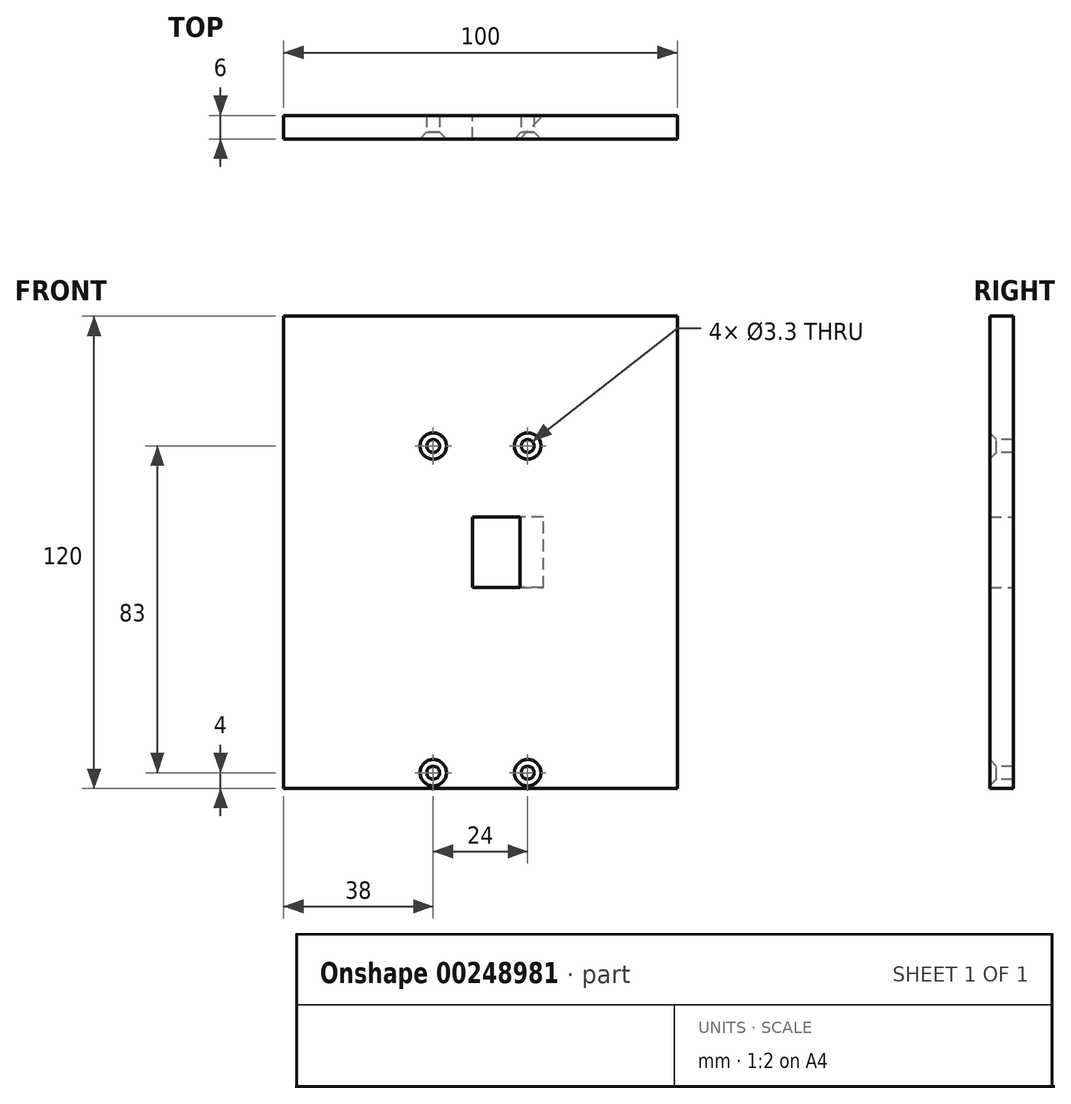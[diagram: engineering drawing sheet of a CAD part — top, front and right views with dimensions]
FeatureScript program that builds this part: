
annotation { "Feature Type Name" : "Feature", "Feature Type Description" : "" }
export const myFeature = defineFeature(function(context is Context, id is Id, definition is map)
    precondition{}
    {
        {
            var Q0;
            Q0=qCreatedBy(makeId("Front.planeOp"),FACE);
            var sketch = newSketch(context, id + "F0", { "sketchPlane" : qUnion([Q0])});
            skLineSegment(sketch, "E0.bottom", {"start": v(50, 60) * mm, "end": v(-50, 60) * mm});
            skLineSegment(sketch, "E0.top", {"start": v(50, -60) * mm, "end": v(-50, -60) * mm});
            skLineSegment(sketch, "E0.left", {"start": v(50, 60) * mm, "end": v(50, -60) * mm});
            skLineSegment(sketch, "E0.right", {"start": v(-50, 60) * mm, "end": v(-50, -60) * mm});
            skPoint(sketch, "E0.middle", {"position": v(0, 0) * mm});
            skLineSegment(sketch, "E1.bottom", {"start": v(10, -9) * mm, "end": v(-2, -9) * mm});
            skLineSegment(sketch, "E1.top", {"start": v(10, 9) * mm, "end": v(-2, 9) * mm});
            skLineSegment(sketch, "E1.left", {"start": v(10, -9) * mm, "end": v(10, 9) * mm});
            skLineSegment(sketch, "E1.right", {"start": v(-2, -9) * mm, "end": v(-2, 9) * mm});
            skPoint(sketch, "E1.middle", {"position": v(4, 0) * mm});
            skSolve(sketch);
        }
        {
            var Q0;
            Q0=makeQuery(id+"F0.imprint","IMPRINT",FACE,{"disambiguationData":[TD([[makeQuery(id+"F0.imprint","IMPRINT",EDGE,{"derivedFrom":sQuery(id+"F0.wireOp",EDGE,"E0.bottom")}),1.0]])]});
            extrude(context, id + "F1", {"entities" : qUnion([Q0]), "endBound" : BoundingType.SYMMETRIC, "depth" : 6 * mm});
        }
        {
            var Q0;
            Q0=makeQuery(id+"F1.opExtrude","CAP_EDGE",EDGE,{"disambiguationData":[OSD([sQuery(id+"F0.wireOp",EDGE,"E1.left")])],"isStart":true});
            chamfer(context, id + "F2", {"entities" : qUnion([Q0]), "width" : 6 * mm, "tangentPropagation" : true});
        }
        {
            var Q0;
            Q0=makeQuery(id+"F1.opExtrude","CAP_FACE",FACE,{"disambiguationData":[OSD([sQuery(id+"F0.wireOp",EDGE,"E0.bottom"),sQuery(id+"F0.wireOp",EDGE,"E0.top"),sQuery(id+"F0.wireOp",EDGE,"E0.left"),sQuery(id+"F0.wireOp",EDGE,"E0.right"),sQuery(id+"F0.wireOp",EDGE,"E1.bottom"),sQuery(id+"F0.wireOp",EDGE,"E1.top"),sQuery(id+"F0.wireOp",EDGE,"E1.left"),sQuery(id+"F0.wireOp",EDGE,"E1.right")])],"isStart":false});
            var sketch = newSketch(context, id + "F3", { "sketchPlane" : qUnion([Q0])});
            skPoint(sketch, "E2", {"position": v(-12, -56) * mm});
            skPoint(sketch, "E3", {"position": v(12, -56) * mm});
            skPoint(sketch, "E4", {"position": v(-12, 27) * mm});
            skPoint(sketch, "E5", {"position": v(12, 27) * mm});
            skSolve(sketch);
        }
        {
            var Q0;
            Q0=sQuery(id+"F3.wireOp",VERTEX,"E4");
            var Q1;
            Q1=sQuery(id+"F3.wireOp",VERTEX,"E5");
            var Q2;
            Q2=sQuery(id+"F3.wireOp",VERTEX,"E3");
            var Q3;
            Q3=sQuery(id+"F3.wireOp",VERTEX,"E2");
            var Q4;
            Q4=makeQuery(id+"F1.opExtrude","SWEPT_BODY",BODY,{"disambiguationData":[OSD([sQuery(id+"F0.wireOp",EDGE,"E0.bottom"),sQuery(id+"F0.wireOp",EDGE,"E0.top"),sQuery(id+"F0.wireOp",EDGE,"E0.left"),sQuery(id+"F0.wireOp",EDGE,"E0.right"),sQuery(id+"F0.wireOp",EDGE,"E1.bottom"),sQuery(id+"F0.wireOp",EDGE,"E1.top"),sQuery(id+"F0.wireOp",EDGE,"E1.left"),sQuery(id+"F0.wireOp",EDGE,"E1.right")])]});
            hole(context, id + "F4", {"style" : HoleStyle.C_SINK, "endStyle" : HoleEndStyle.THROUGH, "standardTappedOrClearance" : lookupTablePath({ "standard" : "ISO", "fit" : "Normal", "size" : "M3", "type" : "Clearance" }), "standardBlindInLast" : lookupTablePath({ "fit" : "Standard", "standard" : "ISO", "size" : "M3", "type" : "Clearance" }), "holeDiameter" : 3.3 * mm, "cSinkDiameter" : 6.72 * mm, "cSinkAngle" : 90 * degree, "tappedDepth" : 4.75 * mm, "tapClearance" : 3, "startFromSketch" : true, "locations" : qUnion([Q0, Q1, Q2, Q3]), "scope" : qUnion([Q4])});
        }
    });
